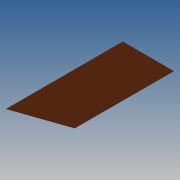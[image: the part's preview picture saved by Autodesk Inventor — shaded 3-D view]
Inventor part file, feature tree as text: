
AUTODESK INVENTOR PART (.ipt)
format: ipt  version: 2013 (Build 170138000, 138)  size: 72,704 bytes
history: native  units: in
note: dims shown in document units (in); Inventor stores cm internally (conversion verified against a paired STEP export)
features: extrude x1, sketch x1
ambient origin geometry x8: Origin, YZ Plane, XZ Plane, XY Plane, X Axis, Y Axis, Z Axis, Center Point
bodies: Solid1 (feature_tree)
feature tree (2):
  extrude  "Extrusion1"  Depth=169.0in
  sketch  "Sketch1"  dims[d0=87.0in d1=169.0in d2=0.5in d3=0.0in d4=30.0in]
